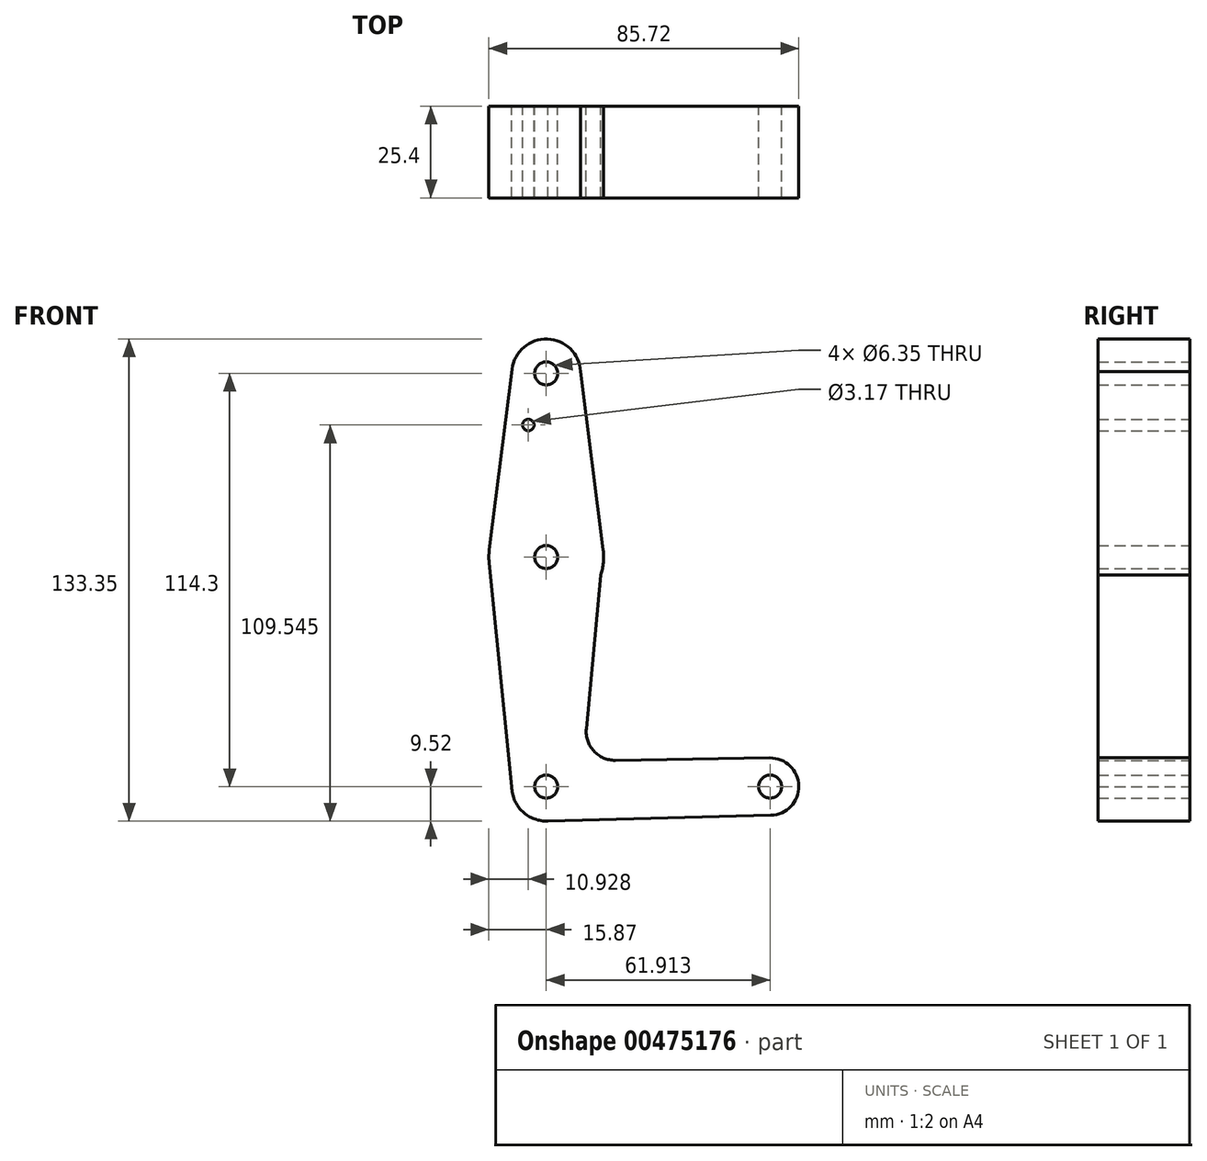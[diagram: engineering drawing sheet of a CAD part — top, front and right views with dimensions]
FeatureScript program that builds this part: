
annotation { "Feature Type Name" : "Feature", "Feature Type Description" : "" }
export const myFeature = defineFeature(function(context is Context, id is Id, definition is map)
    precondition{}
    {
        {
            var Q0;
            Q0=qCreatedBy(makeId("Front.planeOp"),FACE);
            var sketch = newSketch(context, id + "F0", { "sketchPlane" : qUnion([Q0])});
            skLineSegment(sketch, "E0", {"start": v(0, 0) * mm, "end": v(0, 63.5) * mm});
            skLineSegment(sketch, "E1", {"start": v(0, 114.3) * mm, "end": v(0, 63.5) * mm});
            skLineSegment(sketch, "E2", {"start": v(0, 0) * mm, "end": v(61.91, 0) * mm});
            skCircle(sketch, "E3", {"center": v(0, 0) * mm, "radius": 9.53 * mm});
            skCircle(sketch, "E4", {"center": v(61.91, 0) * mm, "radius": 7.94 * mm});
            skCircle(sketch, "E5", {"center": v(0, 63.5) * mm, "radius": 15.88 * mm});
            skCircle(sketch, "E6", {"center": v(0, 114.3) * mm, "radius": 9.53 * mm});
            skLineSegment(sketch, "E7", {"start": v(9.5, 114.85) * mm, "end": v(15.75, 65.5) * mm});
            skLineSegment(sketch, "E8", {"start": v(-15.76, 65.4) * mm, "end": v(-9.45, 115.5) * mm});
            skLineSegment(sketch, "E9", {"start": v(19.11, 7.29) * mm, "end": v(61.8, 7.94) * mm});
            skLineSegment(sketch, "E10", {"start": v(0, -9.53) * mm, "end": v(62.12, -7.93) * mm});
            skLineSegment(sketch, "E11", {"start": v(15.1, 58.57) * mm, "end": v(11.07, 15.98) * mm});
            skCircle(sketch, "E12", {"center": v(0, 0) * mm, "radius": 3.18 * mm});
            skCircle(sketch, "E13", {"center": v(61.91, 0) * mm, "radius": 3.18 * mm});
            skCircle(sketch, "E14", {"center": v(0, 63.5) * mm, "radius": 3.18 * mm});
            skCircle(sketch, "E15", {"center": v(0, 114.3) * mm, "radius": 3.18 * mm});
            skArc(sketch, "E16.filletArc", {"start": v(11.07, 15.98) * mm, "mid": v(13.15, 9.84) * mm, "end": v(19.11, 7.29) * mm});
            skLineSegment(sketch, "E17", {"start": v(-9.52, 0) * mm, "end": v(-15.8, 61.9) * mm});
            skCircle(sketch, "E18", {"center": v(-4.94, 100.03) * mm, "radius": 1.59 * mm});
            skSolve(sketch);
        }
        {
            var Q0;
            Q0 = qSketchRegion(id + "F0", true);
            var Q1;
            {var subQ0=sQuery(id+"F0.wireOp",EDGE,"E12");var subQ1=sQuery(id+"F0.wireOp",EDGE,"E0");var subQ2=makeQuery(id+"F0.imprint","INTERSECT",VERTEX,{"derivedFrom":[subQ1,subQ0]});Q1=makeQuery(id+"F0.imprint","IMPRINT",FACE,{"disambiguationData":[TD([[makeQuery(id+"F0.imprint","IMPRINT",EDGE,{"disambiguationData":[TD([[subQ2,-1.0]])],"derivedFrom":subQ1}),-1.0]])]});}
            extrude(context, id + "F1", {"entities" : qUnion([Q0, Q1]), "depth" : 25.4 * mm});
        }
    });
